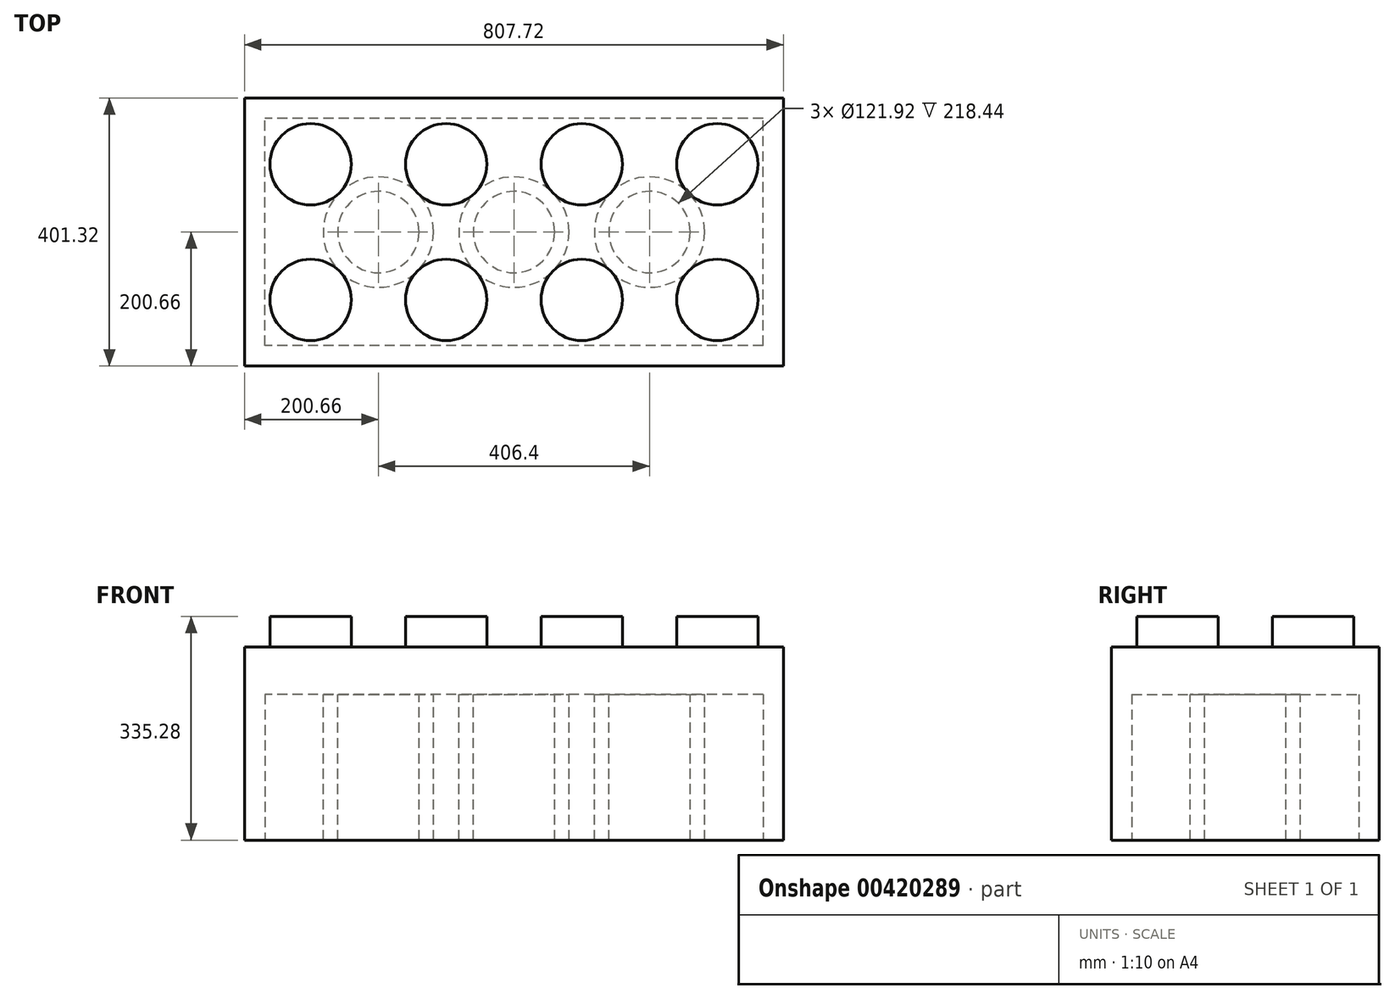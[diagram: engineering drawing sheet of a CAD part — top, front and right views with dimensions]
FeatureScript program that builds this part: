
annotation { "Feature Type Name" : "Feature", "Feature Type Description" : "" }
export const myFeature = defineFeature(function(context is Context, id is Id, definition is map)
    precondition{}
    {
        {
            var Q0;
            Q0=qCreatedBy(makeId("Top.planeOp"),FACE);
            var sketch = newSketch(context, id + "F0", { "sketchPlane" : qUnion([Q0])});
            skLineSegment(sketch, "E0.bottom", {"start": v(403.86, 200.66) * mm, "end": v(-403.86, 200.66) * mm});
            skLineSegment(sketch, "E0.top", {"start": v(403.86, -200.66) * mm, "end": v(-403.86, -200.66) * mm});
            skLineSegment(sketch, "E0.left", {"start": v(403.86, 200.66) * mm, "end": v(403.86, -200.66) * mm});
            skLineSegment(sketch, "E0.right", {"start": v(-403.86, 200.66) * mm, "end": v(-403.86, -200.66) * mm});
            skPoint(sketch, "E0.middle", {"position": v(0, 0) * mm});
            skSolve(sketch);
        }
        {
            var Q0;
            Q0=makeQuery(id+"F0.imprint","IMPRINT",FACE,{"disambiguationData":[TD([[makeQuery(id+"F0.imprint","IMPRINT",EDGE,{"derivedFrom":sQuery(id+"F0.wireOp",EDGE,"E0.bottom")}),1.0]])]});
            extrude(context, id + "F1", {"entities" : qUnion([Q0]), "depth" : 289.56 * mm});
        }
        {
            var Q0;
            Q0=makeQuery(id+"F1.opExtrude","CAP_FACE",FACE,{"disambiguationData":[OSD([sQuery(id+"F0.wireOp",EDGE,"E0.bottom"),sQuery(id+"F0.wireOp",EDGE,"E0.top"),sQuery(id+"F0.wireOp",EDGE,"E0.left"),sQuery(id+"F0.wireOp",EDGE,"E0.right")])],"isStart":false});
            var sketch = newSketch(context, id + "F2", { "sketchPlane" : qUnion([Q0])});
            skCircle(sketch, "E1", {"center": v(-304.8, -101.6) * mm, "radius": 60.96 * mm});
            skCircle(sketch, "E2.1.0.0", {"center": v(-101.6, -101.6) * mm, "radius": 60.96 * mm});
            skCircle(sketch, "E2.2.0.0", {"center": v(101.6, -101.6) * mm, "radius": 60.96 * mm});
            skCircle(sketch, "E2.3.0.0", {"center": v(304.8, -101.6) * mm, "radius": 60.96 * mm});
            skLineSegment(sketch, "E2.direction1", {"start": v(-304.8, -101.6) * mm, "end": v(-101.6, -101.6) * mm, "construction": true});
            skCircle(sketch, "E3.0.1.0", {"center": v(-304.8, 101.6) * mm, "radius": 60.96 * mm});
            skLineSegment(sketch, "E3.direction1", {"start": v(-304.8, -101.6) * mm, "end": v(-304.8, -101.6) * mm});
            skLineSegment(sketch, "E3.direction2", {"start": v(-304.8, -101.6) * mm, "end": v(-304.8, 101.6) * mm, "construction": true});
            skCircle(sketch, "E4.1.0.0", {"center": v(-101.6, 101.6) * mm, "radius": 60.96 * mm});
            skCircle(sketch, "E4.2.0.0", {"center": v(101.6, 101.6) * mm, "radius": 60.96 * mm});
            skCircle(sketch, "E4.3.0.0", {"center": v(304.8, 101.6) * mm, "radius": 60.96 * mm});
            skLineSegment(sketch, "E4.direction1", {"start": v(-304.8, 101.6) * mm, "end": v(-101.6, 101.6) * mm, "construction": true});
            skSolve(sketch);
        }
        {
            var Q0;
            Q0=makeQuery(id+"F2.imprint","IMPRINT",FACE,{"disambiguationData":[TD([[makeQuery(id+"F2.imprint","IMPRINT",EDGE,{"derivedFrom":sQuery(id+"F2.wireOp",EDGE,"E1")}),1.0]])]});
            var Q1;
            Q1=makeQuery(id+"F2.imprint","IMPRINT",FACE,{"disambiguationData":[TD([[makeQuery(id+"F2.imprint","IMPRINT",EDGE,{"derivedFrom":sQuery(id+"F2.wireOp",EDGE,"E3.0.1.0")}),1.0]])]});
            var Q2;
            Q2=makeQuery(id+"F2.imprint","IMPRINT",FACE,{"disambiguationData":[TD([[makeQuery(id+"F2.imprint","IMPRINT",EDGE,{"derivedFrom":sQuery(id+"F2.wireOp",EDGE,"E4.1.0.0")}),1.0]])]});
            var Q3;
            Q3=makeQuery(id+"F2.imprint","IMPRINT",FACE,{"disambiguationData":[TD([[makeQuery(id+"F2.imprint","IMPRINT",EDGE,{"derivedFrom":sQuery(id+"F2.wireOp",EDGE,"E2.1.0.0")}),1.0]])]});
            var Q4;
            Q4=makeQuery(id+"F2.imprint","IMPRINT",FACE,{"disambiguationData":[TD([[makeQuery(id+"F2.imprint","IMPRINT",EDGE,{"derivedFrom":sQuery(id+"F2.wireOp",EDGE,"E2.2.0.0")}),1.0]])]});
            var Q5;
            Q5=makeQuery(id+"F2.imprint","IMPRINT",FACE,{"disambiguationData":[TD([[makeQuery(id+"F2.imprint","IMPRINT",EDGE,{"derivedFrom":sQuery(id+"F2.wireOp",EDGE,"E4.2.0.0")}),1.0]])]});
            var Q6;
            Q6=makeQuery(id+"F2.imprint","IMPRINT",FACE,{"disambiguationData":[TD([[makeQuery(id+"F2.imprint","IMPRINT",EDGE,{"derivedFrom":sQuery(id+"F2.wireOp",EDGE,"E4.3.0.0")}),1.0]])]});
            var Q7;
            Q7=makeQuery(id+"F2.imprint","IMPRINT",FACE,{"disambiguationData":[TD([[makeQuery(id+"F2.imprint","IMPRINT",EDGE,{"derivedFrom":sQuery(id+"F2.wireOp",EDGE,"E2.3.0.0")}),1.0]])]});
            extrude(context, id + "F3", {"entities" : qUnion([Q0, Q1, Q2, Q3, Q4, Q5, Q6, Q7]), "operationType" : NewBodyOperationType.ADD, "depth" : 45.72 * mm});
        }
        {
            var Q0;
            Q0=makeQuery(id+"F1.opExtrude","CAP_FACE",FACE,{"disambiguationData":[OSD([sQuery(id+"F0.wireOp",EDGE,"E0.bottom"),sQuery(id+"F0.wireOp",EDGE,"E0.top"),sQuery(id+"F0.wireOp",EDGE,"E0.left"),sQuery(id+"F0.wireOp",EDGE,"E0.right")])],"isStart":true});
            var sketch = newSketch(context, id + "F4", { "sketchPlane" : qUnion([Q0])});
            skLineSegment(sketch, "E5.bottom", {"start": v(373.38, 170.18) * mm, "end": v(-373.38, 170.18) * mm});
            skLineSegment(sketch, "E5.top", {"start": v(373.38, -170.18) * mm, "end": v(-373.38, -170.18) * mm});
            skLineSegment(sketch, "E5.left", {"start": v(373.38, 170.18) * mm, "end": v(373.38, -170.18) * mm});
            skLineSegment(sketch, "E5.right", {"start": v(-373.38, 170.18) * mm, "end": v(-373.38, -170.18) * mm});
            skPoint(sketch, "E5.middle", {"position": v(0, 0) * mm});
            skSolve(sketch);
        }
        {
            var Q0;
            Q0=makeQuery(id+"F4.imprint","IMPRINT",FACE,{"disambiguationData":[TD([[makeQuery(id+"F4.imprint","IMPRINT",EDGE,{"derivedFrom":sQuery(id+"F4.wireOp",EDGE,"E5.bottom")}),1.0]])]});
            extrude(context, id + "F5", {"entities" : qUnion([Q0]), "operationType" : NewBodyOperationType.REMOVE, "oppositeDirection" : true, "depth" : 218.44 * mm});
        }
        {
            var Q0;
            Q0=makeQuery(id+"F5.boolean.opBoolean","COPY",FACE,{"derivedFrom":makeQuery(id+"F5.opExtrude","CAP_FACE",FACE,{"disambiguationData":[OSD([sQuery(id+"F4.wireOp",EDGE,"E5.bottom"),sQuery(id+"F4.wireOp",EDGE,"E5.top"),sQuery(id+"F4.wireOp",EDGE,"E5.left"),sQuery(id+"F4.wireOp",EDGE,"E5.right")])],"isStart":false})});
            var sketch = newSketch(context, id + "F6", { "sketchPlane" : qUnion([Q0])});
            skCircle(sketch, "E6", {"center": v(0, 0) * mm, "radius": 82.68 * mm});
            skCircle(sketch, "E7", {"center": v(0, 0) * mm, "radius": 60.96 * mm});
            skCircle(sketch, "E8.1.0.0", {"center": v(203.2, 0) * mm, "radius": 60.96 * mm});
            skCircle(sketch, "E8.1.0.1", {"center": v(203.2, 0) * mm, "radius": 82.68 * mm});
            skLineSegment(sketch, "E8.direction1", {"start": v(0, 0) * mm, "end": v(203.2, 0) * mm, "construction": true});
            skCircle(sketch, "E9.1.0.0", {"center": v(-203.2, 0) * mm, "radius": 60.96 * mm});
            skCircle(sketch, "E9.1.0.1", {"center": v(-203.2, 0) * mm, "radius": 82.68 * mm});
            skLineSegment(sketch, "E9.direction1", {"start": v(0, 0) * mm, "end": v(-203.2, 0) * mm, "construction": true});
            skSolve(sketch);
        }
        {
            var Q0;
            Q0=makeQuery(id+"F6.imprint","IMPRINT",FACE,{"disambiguationData":[TD([[makeQuery(id+"F6.imprint","IMPRINT",EDGE,{"derivedFrom":sQuery(id+"F6.wireOp",EDGE,"E9.1.0.0")}),-1.0]])]});
            var Q1;
            Q1=makeQuery(id+"F6.imprint","IMPRINT",FACE,{"disambiguationData":[TD([[makeQuery(id+"F6.imprint","IMPRINT",EDGE,{"derivedFrom":sQuery(id+"F6.wireOp",EDGE,"E6")}),1.0]])]});
            var Q2;
            Q2=makeQuery(id+"F6.imprint","IMPRINT",FACE,{"disambiguationData":[TD([[makeQuery(id+"F6.imprint","IMPRINT",EDGE,{"derivedFrom":sQuery(id+"F6.wireOp",EDGE,"E8.1.0.0")}),-1.0]])]});
            extrude(context, id + "F7", {"entities" : qUnion([Q0, Q1, Q2]), "operationType" : NewBodyOperationType.ADD, "depth" : 218.44 * mm});
        }
    });
